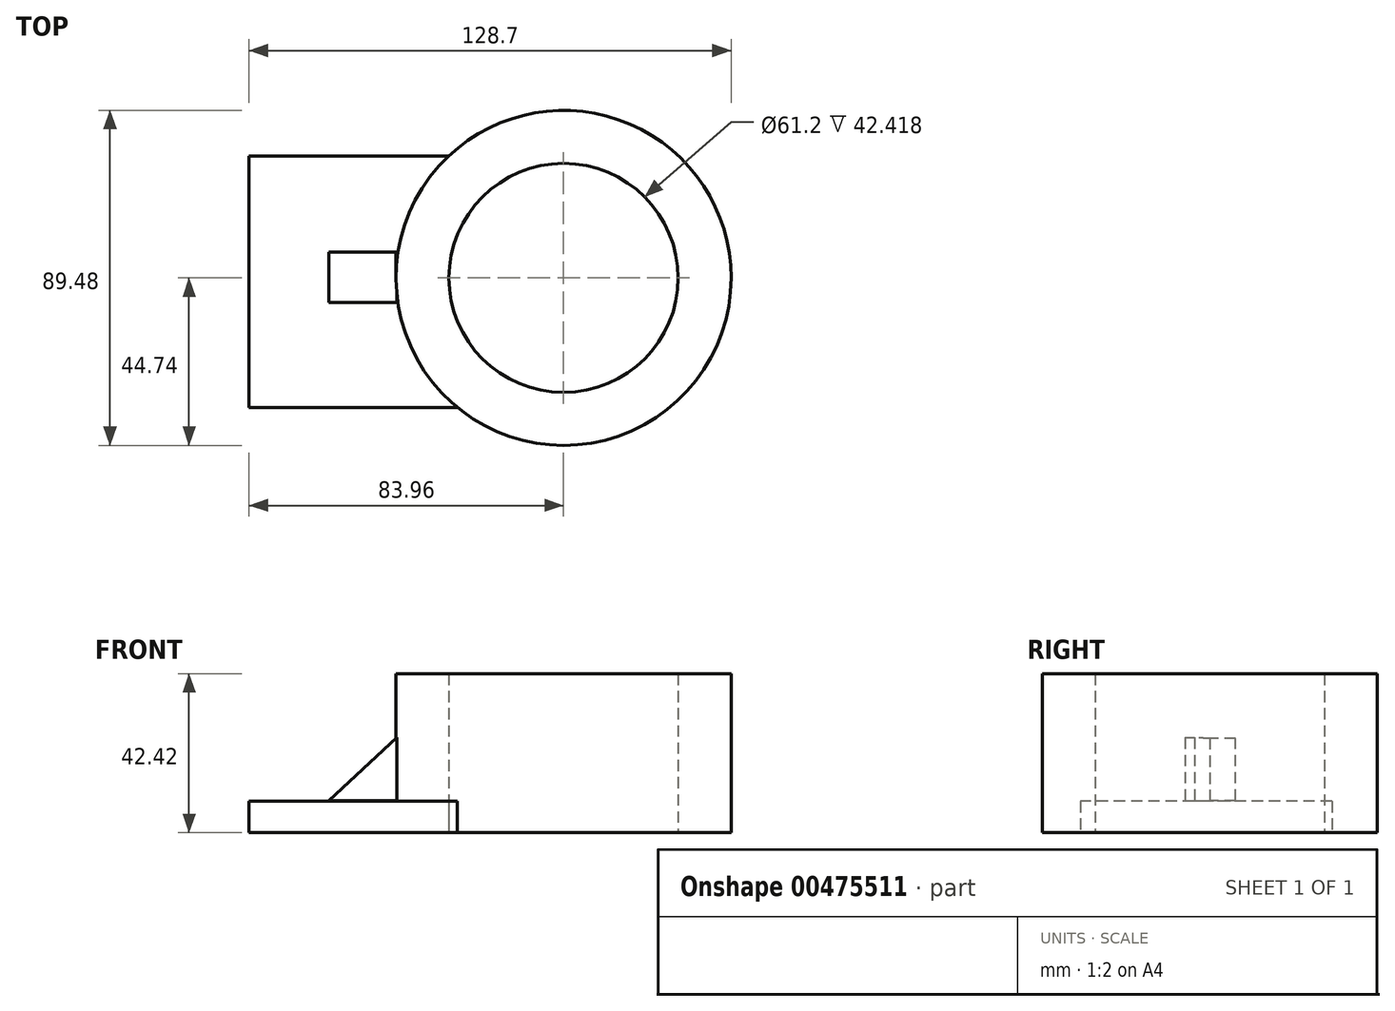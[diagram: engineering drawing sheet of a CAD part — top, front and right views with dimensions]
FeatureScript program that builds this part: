
annotation { "Feature Type Name" : "Feature", "Feature Type Description" : "" }
export const myFeature = defineFeature(function(context is Context, id is Id, definition is map)
    precondition{}
    {
        {
            var Q0;
            Q0=qCreatedBy(makeId("Top.planeOp"),FACE);
            var sketch = newSketch(context, id + "F0", { "sketchPlane" : qUnion([Q0])});
            skCircle(sketch, "E0", {"center": v(0, 0) * mm, "radius": 44.74 * mm});
            skCircle(sketch, "E1", {"center": v(0, 0) * mm, "radius": 30.6 * mm});
            skLineSegment(sketch, "E2", {"start": v(-30.66, 32.58) * mm, "end": v(-83.96, 32.58) * mm});
            skLineSegment(sketch, "E3", {"start": v(-83.96, 32.58) * mm, "end": v(-83.96, -34.57) * mm});
            skLineSegment(sketch, "E4", {"start": v(-83.96, -34.57) * mm, "end": v(-28.39, -34.57) * mm});
            skLineSegment(sketch, "E5", {"start": v(0, 0) * mm, "end": v(-100.75, 0) * mm, "construction": true});
            skSolve(sketch);
        }
        {
            var Q0;
            Q0=makeQuery(id+"F0.imprint","IMPRINT",FACE,{"disambiguationData":[TD([[makeQuery(id+"F0.imprint","IMPRINT",EDGE,{"derivedFrom":sQuery(id+"F0.wireOp",EDGE,"E1")}),-1.0]])]});
            extrude(context, id + "F1", {"entities" : qUnion([Q0]), "depth" : 42.42 * mm});
        }
        {
            var Q0;
            {var subQ0=sQuery(id+"F0.wireOp",EDGE,"E2");Q0=makeQuery(id+"F0.imprint","IMPRINT",FACE,{"disambiguationData":[TD([[makeQuery(id+"F0.imprint","IMPRINT",EDGE,{"derivedFrom":subQ0}),1.0]])]});}
            extrude(context, id + "F2", {"entities" : qUnion([Q0]), "operationType" : NewBodyOperationType.ADD, "depth" : 8.38 * mm});
        }
        {
            var Q0;
            Q0=qCreatedBy(makeId("Front.planeOp"),FACE);
            var sketch = newSketch(context, id + "F3", { "sketchPlane" : qUnion([Q0])});
            skLineSegment(sketch, "E6", {"start": v(-44.54, 25.35) * mm, "end": v(-44.54, 8.56) * mm});
            skLineSegment(sketch, "E7", {"start": v(-44.54, 8.56) * mm, "end": v(-62.65, 8.56) * mm});
            skLineSegment(sketch, "E8", {"start": v(-62.65, 8.56) * mm, "end": v(-44.54, 25.35) * mm});
            skSolve(sketch);
        }
        {
            var Q0;
            Q0=makeQuery(id+"F3.imprint","IMPRINT",FACE,{"disambiguationData":[TD([[makeQuery(id+"F3.imprint","IMPRINT",EDGE,{"derivedFrom":sQuery(id+"F3.wireOp",EDGE,"E6")}),-1.0]])]});
            extrude(context, id + "F4", {"entities" : qUnion([Q0]), "operationType" : NewBodyOperationType.ADD, "depth" : 6.6 * mm});
        }
        {
            var Q0;
            Q0=makeQuery(id+"F4.opExtrude","CAP_FACE",FACE,{"disambiguationData":[OSD([sQuery(id+"F3.wireOp",EDGE,"E6"),sQuery(id+"F3.wireOp",EDGE,"E7"),sQuery(id+"F3.wireOp",EDGE,"E8")])],"isStart":true});
            extrude(context, id + "F5", {"entities" : qUnion([Q0]), "operationType" : NewBodyOperationType.ADD, "depth" : 6.86 * mm});
        }
    });
